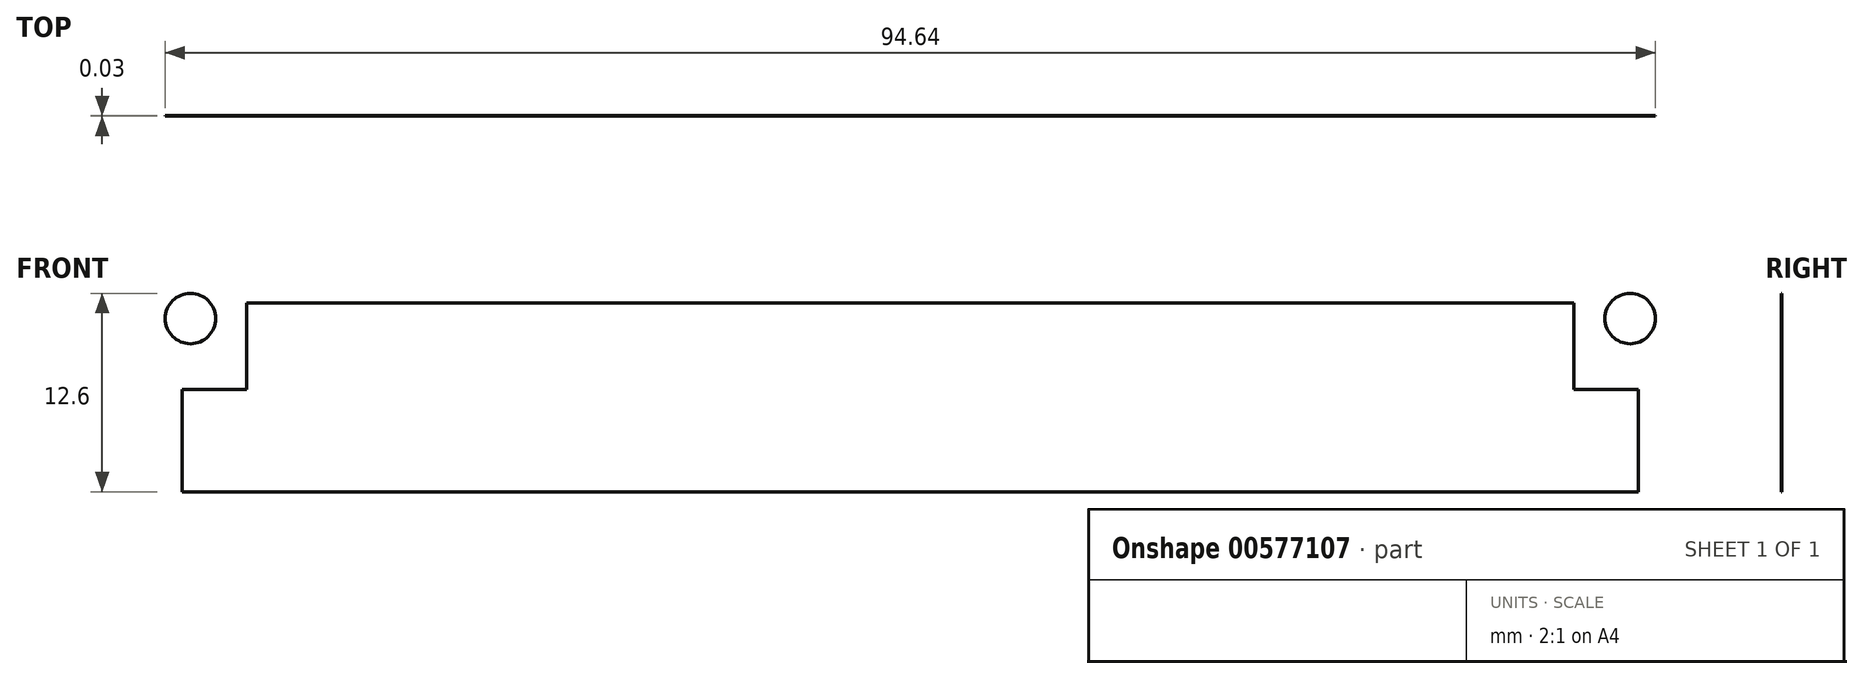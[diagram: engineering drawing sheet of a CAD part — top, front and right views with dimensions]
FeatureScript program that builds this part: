
annotation { "Feature Type Name" : "Feature", "Feature Type Description" : "" }
export const myFeature = defineFeature(function(context is Context, id is Id, definition is map)
    precondition{}
    {
        {
            var Q0;
            Q0=qCreatedBy(makeId("Front.planeOp"),FACE);
            var sketch = newSketch(context, id + "F0", { "sketchPlane" : qUnion([Q0])});
            skLineSegment(sketch, "E0.bottom", {"start": v(0, 0) * mm, "end": v(92.5, 0) * mm});
            skLineSegment(sketch, "E0.top", {"start": v(0, 6.5) * mm, "end": v(92.5, 6.5) * mm});
            skLineSegment(sketch, "E0.left", {"start": v(0, 0) * mm, "end": v(0, 6.5) * mm});
            skLineSegment(sketch, "E0.right", {"start": v(92.5, 0) * mm, "end": v(92.5, 6.5) * mm});
            skLineSegment(sketch, "E1.bottom", {"start": v(4.1, 6.5) * mm, "end": v(88.4, 6.5) * mm});
            skLineSegment(sketch, "E1.top", {"start": v(4.1, 12) * mm, "end": v(88.4, 12) * mm});
            skLineSegment(sketch, "E1.left", {"start": v(88.4, 6.5) * mm, "end": v(88.4, 12) * mm});
            skLineSegment(sketch, "E1.right", {"start": v(4.1, 6.5) * mm, "end": v(4.1, 12) * mm});
            skLineSegment(sketch, "E2", {"start": v(46.25, 0) * mm, "end": v(46.25, 12) * mm, "construction": true});
            skCircle(sketch, "E3", {"center": v(0.53, 11) * mm, "radius": 1.6 * mm});
            skCircle(sketch, "E4", {"center": v(91.97, 11) * mm, "radius": 1.6 * mm});
            skLineSegment(sketch, "E5", {"start": v(0.53, 11) * mm, "end": v(91.97, 11) * mm, "construction": true});
            skSolve(sketch);
        }
        {
            var Q0;
            Q0 = qSketchRegion(id + "F0", true);
            extrude(context, id + "F1", {"entities" : qUnion([Q0]), "depth" : 0.03 * mm, "offsetDistance" : 25.4 * mm});
        }
    });
